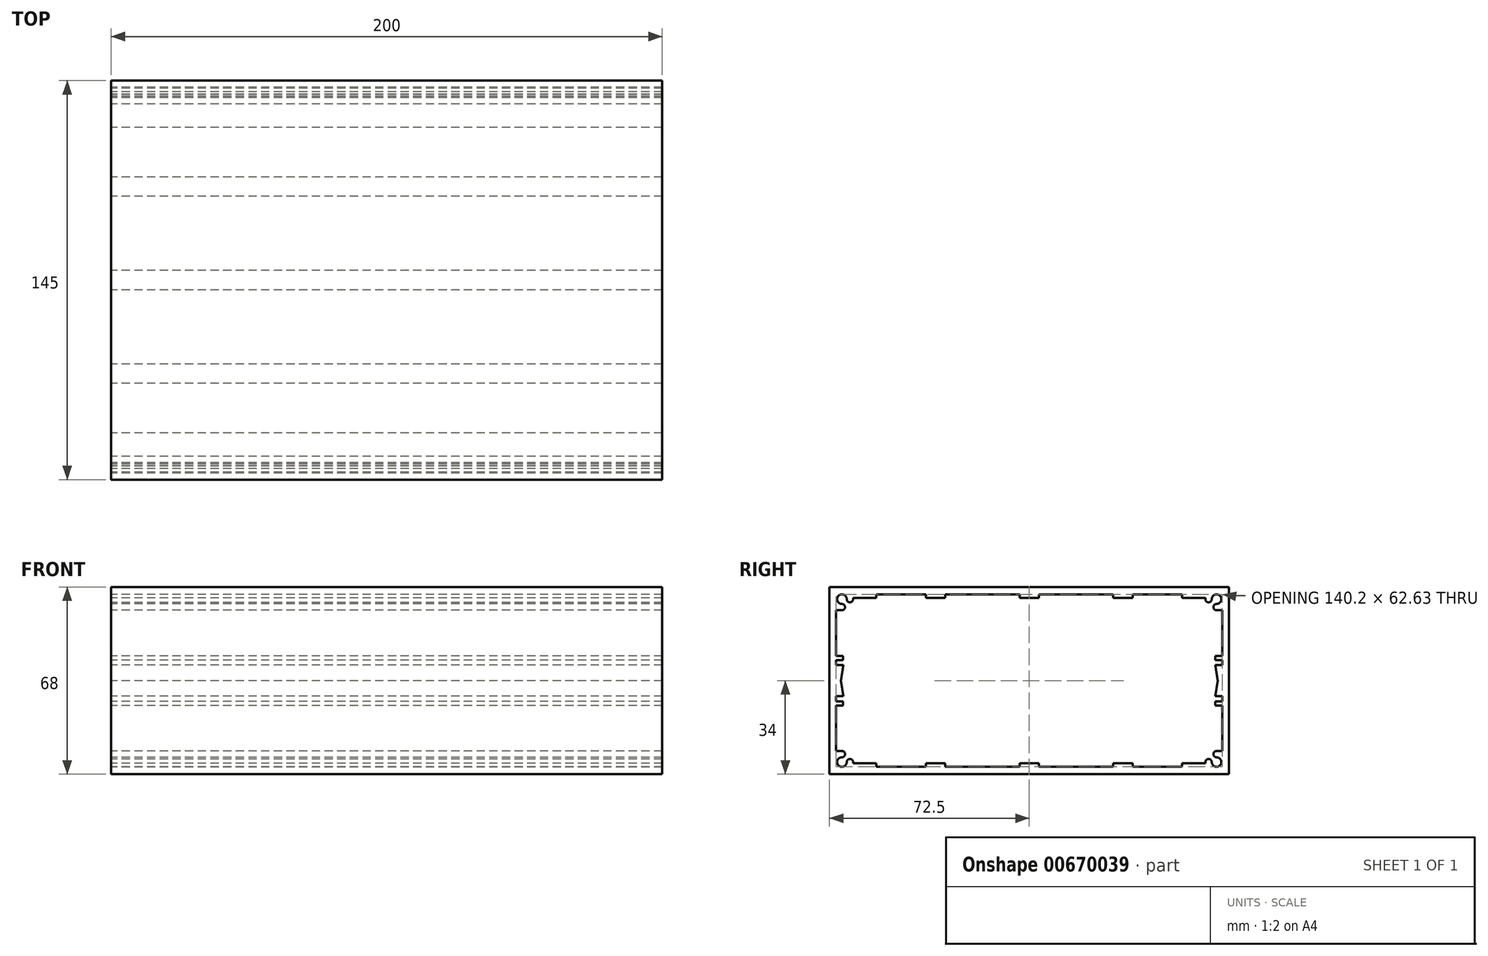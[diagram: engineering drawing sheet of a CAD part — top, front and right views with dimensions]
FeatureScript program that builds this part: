
annotation { "Feature Type Name" : "Feature", "Feature Type Description" : "" }
export const myFeature = defineFeature(function(context is Context, id is Id, definition is map)
    precondition{}
    {
        {
            var Q0;
            Q0=qCreatedBy(makeId("Right.planeOp"),FACE);
            var sketch = newSketch(context, id + "F0", { "sketchPlane" : qUnion([Q0])});
            skLineSegment(sketch, "E0.bottom", {"start": v(0, 0) * mm, "end": v(145, 0) * mm});
            skLineSegment(sketch, "E0.top", {"start": v(0, 68) * mm, "end": v(145, 68) * mm});
            skLineSegment(sketch, "E0.left", {"start": v(0, 0) * mm, "end": v(0, 68) * mm});
            skLineSegment(sketch, "E0.right", {"start": v(145, 0) * mm, "end": v(145, 68) * mm});
            skLineSegment(sketch, "E1", {"start": v(72.5, 68) * mm, "end": v(72.5, 0) * mm, "construction": true});
            skLineSegment(sketch, "E2", {"start": v(0, 34) * mm, "end": v(145, 34) * mm, "construction": true});
            skPoint(sketch, "E3.middle", {"position": v(72.5, 34) * mm});
            skLineSegment(sketch, "E4", {"start": v(72.5, 64) * mm, "end": v(69, 64) * mm});
            skLineSegment(sketch, "E5", {"start": v(69, 64) * mm, "end": v(69, 65.3) * mm});
            skLineSegment(sketch, "E6", {"start": v(69, 65.3) * mm, "end": v(42, 65.3) * mm});
            skLineSegment(sketch, "E7", {"start": v(42, 65.3) * mm, "end": v(42, 64) * mm});
            skLineSegment(sketch, "E8", {"start": v(42, 64) * mm, "end": v(35, 64) * mm});
            skLineSegment(sketch, "E9", {"start": v(35, 64) * mm, "end": v(35, 65.3) * mm});
            skLineSegment(sketch, "E10", {"start": v(35, 65.3) * mm, "end": v(17, 65.3) * mm});
            skLineSegment(sketch, "E11", {"start": v(17, 65.3) * mm, "end": v(17, 64) * mm});
            skLineSegment(sketch, "E12", {"start": v(17, 64) * mm, "end": v(8.55, 64) * mm});
            skArc(sketch, "E13", {"start": v(6.25, 63.6) * mm, "mid": v(3.26, 64.84) * mm, "end": v(4.5, 61.85) * mm});
            skArc(sketch, "E14", {"start": v(6.25, 63.6) * mm, "mid": v(7.4, 62.45) * mm, "end": v(8.55, 63.6) * mm});
            skLineSegment(sketch, "E15", {"start": v(8.55, 63.6) * mm, "end": v(8.55, 64) * mm});
            skArc(sketch, "E16", {"start": v(4.5, 59.55) * mm, "mid": v(5.65, 60.7) * mm, "end": v(4.5, 61.85) * mm});
            skLineSegment(sketch, "E17", {"start": v(4.5, 59.55) * mm, "end": v(2.4, 59.55) * mm});
            skLineSegment(sketch, "E18", {"start": v(2.4, 59.55) * mm, "end": v(2.4, 43) * mm});
            skLineSegment(sketch, "E19", {"start": v(2.4, 43) * mm, "end": v(4.92, 43) * mm});
            skLineSegment(sketch, "E20", {"start": v(4.92, 43) * mm, "end": v(4.92, 41.5) * mm});
            skLineSegment(sketch, "E21", {"start": v(4.92, 41.5) * mm, "end": v(2.4, 41.5) * mm});
            skLineSegment(sketch, "E22", {"start": v(2.4, 41.5) * mm, "end": v(2.4, 39.68) * mm});
            skLineSegment(sketch, "E23", {"start": v(2.4, 39.68) * mm, "end": v(5, 39.68) * mm});
            skLineSegment(sketch, "E24", {"start": v(5, 39.68) * mm, "end": v(4.1, 34) * mm});
            skLineSegment(sketch, "E25.MirrorCS", {"start": v(103, 65.3) * mm, "end": v(103, 64) * mm});
            skLineSegment(sketch, "E26.MirrorCS", {"start": v(142.6, 39.68) * mm, "end": v(140, 39.68) * mm});
            skLineSegment(sketch, "E27.MirrorCS", {"start": v(110, 64) * mm, "end": v(110, 65.3) * mm});
            skLineSegment(sketch, "E28.MirrorCS", {"start": v(128, 65.3) * mm, "end": v(128, 64) * mm});
            skLineSegment(sketch, "E29.MirrorCS", {"start": v(140.08, 41.5) * mm, "end": v(142.6, 41.5) * mm});
            skLineSegment(sketch, "E30.MirrorCS", {"start": v(140.08, 43) * mm, "end": v(140.08, 41.5) * mm});
            skLineSegment(sketch, "E31.MirrorCS", {"start": v(76, 64) * mm, "end": v(76, 65.3) * mm});
            skLineSegment(sketch, "E32.MirrorCS", {"start": v(136.45, 63.6) * mm, "end": v(136.45, 64) * mm});
            skLineSegment(sketch, "E33.MirrorCS", {"start": v(142.6, 59.55) * mm, "end": v(142.6, 43) * mm});
            skLineSegment(sketch, "E34.MirrorCS", {"start": v(140.5, 59.55) * mm, "end": v(142.6, 59.55) * mm});
            skLineSegment(sketch, "E35.MirrorCS", {"start": v(142.6, 41.5) * mm, "end": v(142.6, 39.68) * mm});
            skArc(sketch, "E36.MirrorCS", {"start": v(138.75, 63.6) * mm, "mid": v(137.6, 62.45) * mm, "end": v(136.45, 63.6) * mm});
            skLineSegment(sketch, "E37.MirrorCS", {"start": v(142.6, 43) * mm, "end": v(140.08, 43) * mm});
            skLineSegment(sketch, "E38.MirrorCS", {"start": v(110, 65.3) * mm, "end": v(128, 65.3) * mm});
            skLineSegment(sketch, "E39.MirrorCS", {"start": v(140, 39.68) * mm, "end": v(140.9, 34) * mm});
            skLineSegment(sketch, "E40.MirrorCS", {"start": v(128, 64) * mm, "end": v(136.45, 64) * mm});
            skLineSegment(sketch, "E41.MirrorCS", {"start": v(76, 65.3) * mm, "end": v(103, 65.3) * mm});
            skLineSegment(sketch, "E42.MirrorCS", {"start": v(72.5, 64) * mm, "end": v(76, 64) * mm});
            skLineSegment(sketch, "E43.MirrorCS", {"start": v(103, 64) * mm, "end": v(110, 64) * mm});
            skArc(sketch, "E44.MirrorCS", {"start": v(138.75, 63.6) * mm, "mid": v(141.74, 64.84) * mm, "end": v(140.5, 61.85) * mm});
            skArc(sketch, "E45.MirrorCS", {"start": v(140.5, 59.55) * mm, "mid": v(139.35, 60.7) * mm, "end": v(140.5, 61.85) * mm});
            skLineSegment(sketch, "E46.MirrorCS", {"start": v(2.4, 8.45) * mm, "end": v(2.4, 25) * mm});
            skLineSegment(sketch, "E47.MirrorCS", {"start": v(4.5, 8.45) * mm, "end": v(2.4, 8.45) * mm});
            skLineSegment(sketch, "E48.MirrorCS", {"start": v(5, 19.2) * mm, "end": v(5, 19.21) * mm});
            skArc(sketch, "E49.MirrorCS", {"start": v(138.75, 4.4) * mm, "mid": v(137.6, 5.55) * mm, "end": v(136.45, 4.4) * mm});
            skLineSegment(sketch, "E50.MirrorCS", {"start": v(8.55, 4.4) * mm, "end": v(8.55, 4) * mm});
            skLineSegment(sketch, "E51.MirrorCS", {"start": v(136.45, 4.4) * mm, "end": v(136.45, 4) * mm});
            skLineSegment(sketch, "E52.MirrorCS", {"start": v(72.5, 4) * mm, "end": v(69, 4) * mm});
            skArc(sketch, "E53.MirrorCS", {"start": v(6.25, 4.4) * mm, "mid": v(7.4, 5.55) * mm, "end": v(8.55, 4.4) * mm});
            skLineSegment(sketch, "E54.MirrorCS", {"start": v(69, 4) * mm, "end": v(69, 2.7) * mm});
            skLineSegment(sketch, "E55.MirrorCS", {"start": v(142.6, 25) * mm, "end": v(140.08, 25) * mm});
            skLineSegment(sketch, "E56.MirrorCS", {"start": v(4.92, 26.5) * mm, "end": v(2.4, 26.5) * mm});
            skArc(sketch, "E57.MirrorCS", {"start": v(4.5, 8.45) * mm, "mid": v(5.65, 7.3) * mm, "end": v(4.5, 6.15) * mm});
            skLineSegment(sketch, "E58.MirrorCS", {"start": v(140.08, 25) * mm, "end": v(140.08, 26.5) * mm});
            skLineSegment(sketch, "E59.MirrorCS", {"start": v(2.4, 28.32) * mm, "end": v(5, 28.32) * mm});
            skLineSegment(sketch, "E60.MirrorCS", {"start": v(4.92, 25) * mm, "end": v(4.92, 26.5) * mm});
            skLineSegment(sketch, "E61.MirrorCS", {"start": v(140.5, 8.45) * mm, "end": v(142.6, 8.45) * mm});
            skLineSegment(sketch, "E62.MirrorCS", {"start": v(140.08, 26.5) * mm, "end": v(142.6, 26.5) * mm});
            skLineSegment(sketch, "E63.MirrorCS", {"start": v(72.5, 4) * mm, "end": v(76, 4) * mm});
            skLineSegment(sketch, "E64.MirrorCS", {"start": v(142.6, 8.45) * mm, "end": v(142.6, 25) * mm});
            skLineSegment(sketch, "E65.MirrorCS", {"start": v(2.4, 25) * mm, "end": v(4.92, 25) * mm});
            skLineSegment(sketch, "E66.MirrorCS", {"start": v(128, 2.7) * mm, "end": v(128, 4) * mm});
            skLineSegment(sketch, "E67.MirrorCS", {"start": v(2.4, 26.5) * mm, "end": v(2.4, 28.32) * mm});
            skLineSegment(sketch, "E68.MirrorCS", {"start": v(103, 2.7) * mm, "end": v(103, 4) * mm});
            skLineSegment(sketch, "E69.MirrorCS", {"start": v(42, 2.7) * mm, "end": v(42, 4) * mm});
            skLineSegment(sketch, "E70.MirrorCS", {"start": v(142.6, 28.32) * mm, "end": v(140, 28.32) * mm});
            skLineSegment(sketch, "E71.MirrorCS", {"start": v(76, 4) * mm, "end": v(76, 2.7) * mm});
            skLineSegment(sketch, "E72.MirrorCS", {"start": v(17, 2.7) * mm, "end": v(17, 4) * mm});
            skLineSegment(sketch, "E73.MirrorCS", {"start": v(110, 4) * mm, "end": v(110, 2.7) * mm});
            skLineSegment(sketch, "E74.MirrorCS", {"start": v(142.6, 26.5) * mm, "end": v(142.6, 28.32) * mm});
            skArc(sketch, "E75.MirrorCS", {"start": v(140.5, 8.45) * mm, "mid": v(139.35, 7.3) * mm, "end": v(140.5, 6.15) * mm});
            skLineSegment(sketch, "E76.MirrorCS", {"start": v(35, 4) * mm, "end": v(35, 2.7) * mm});
            skArc(sketch, "E77.MirrorCS", {"start": v(6.25, 4.4) * mm, "mid": v(3.26, 3.16) * mm, "end": v(4.5, 6.15) * mm});
            skArc(sketch, "E78.MirrorCS", {"start": v(138.75, 4.4) * mm, "mid": v(141.74, 3.16) * mm, "end": v(140.5, 6.15) * mm});
            skLineSegment(sketch, "E79.MirrorCS", {"start": v(5, 28.32) * mm, "end": v(4.1, 34) * mm});
            skLineSegment(sketch, "E80.MirrorCS", {"start": v(140, 28.32) * mm, "end": v(140.9, 34) * mm});
            skLineSegment(sketch, "E81.MirrorCS", {"start": v(17, 4) * mm, "end": v(8.55, 4) * mm});
            skLineSegment(sketch, "E82.MirrorCS", {"start": v(128, 4) * mm, "end": v(136.45, 4) * mm});
            skLineSegment(sketch, "E83.MirrorCS", {"start": v(103, 4) * mm, "end": v(110, 4) * mm});
            skLineSegment(sketch, "E84.MirrorCS", {"start": v(76, 2.7) * mm, "end": v(103, 2.7) * mm});
            skLineSegment(sketch, "E85.MirrorCS", {"start": v(42, 4) * mm, "end": v(35, 4) * mm});
            skLineSegment(sketch, "E86.MirrorCS", {"start": v(35, 2.7) * mm, "end": v(17, 2.7) * mm});
            skLineSegment(sketch, "E87.MirrorCS", {"start": v(110, 2.7) * mm, "end": v(128, 2.7) * mm});
            skLineSegment(sketch, "E88.MirrorCS", {"start": v(69, 2.7) * mm, "end": v(42, 2.7) * mm});
            skSolve(sketch);
        }
        {
            var Q0;
            Q0=qSketchRegion(id+"F0",true);
            extrude(context, id + "F1", {"entities" : qUnion([Q0]), "depth" : 200 * mm, "offsetDistance" : 25 * mm});
        }
    });
